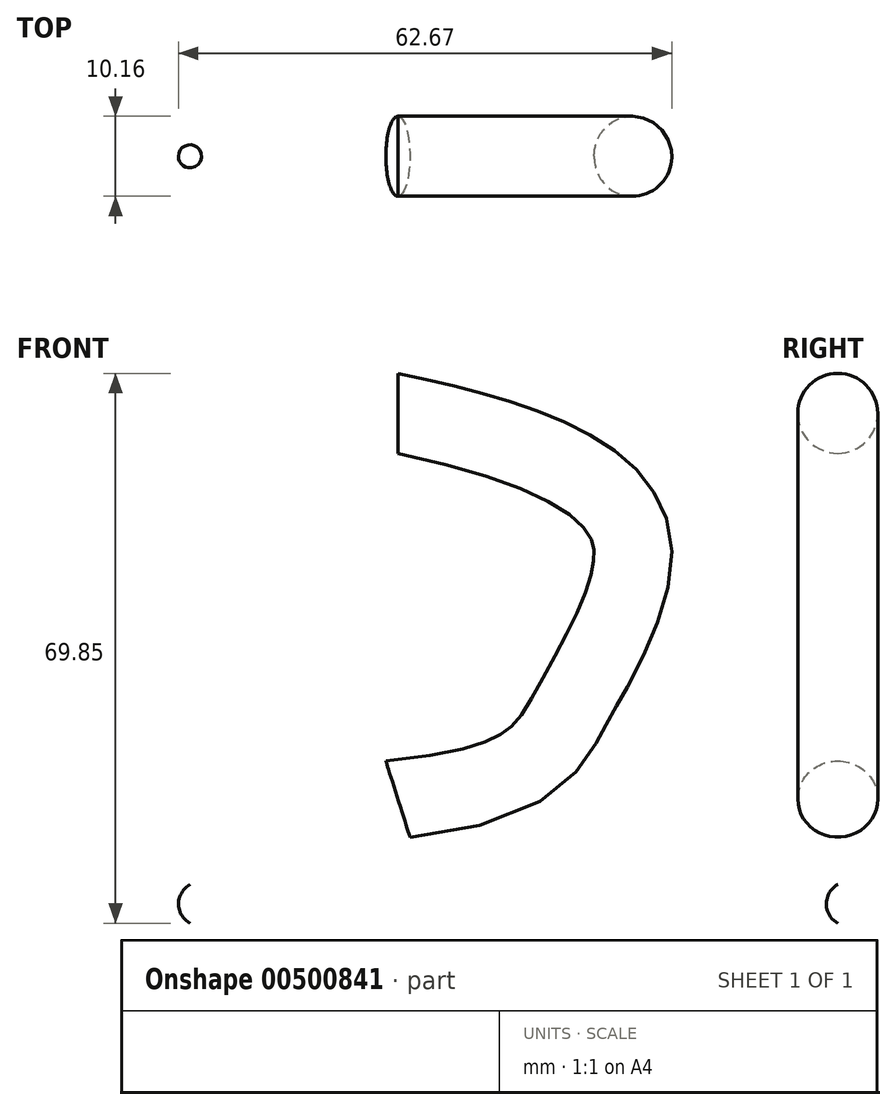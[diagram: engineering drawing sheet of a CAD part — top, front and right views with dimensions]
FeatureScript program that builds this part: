
annotation { "Feature Type Name" : "Feature", "Feature Type Description" : "" }
export const myFeature = defineFeature(function(context is Context, id is Id, definition is map)
    precondition{}
    {
        {
            var Q0;
            Q0=qCreatedBy(makeId("Front.planeOp"),FACE);
            var sketch = newSketch(context, id + "F0", { "sketchPlane" : qUnion([Q0])});
            skFitSpline(sketch, "E0", {"points": [v(0, 0) * mm, v(21.38, 0) * mm, v(22.29, 0) * mm, v(32.23, 23.6) * mm, v(34.34, 76.3) * mm, v(28.91, 76.3) * mm, v(29.21, 58.23) * mm, v(25.9, 24.8) * mm, v(18.37, 6.12) * mm, v(0, 4.92) * mm, v(0, 0) * mm]});
            skLineSegment(sketch, "E1", {"start": v(0, 76.07) * mm, "end": v(0, 0) * mm});
            skSolve(sketch);
        }
        {
            var Q0;
            {var subQ0=sQuery(id+"F0.wireOp",EDGE,"E1");var subQ1=sQuery(id+"F0.wireOp",EDGE,"E0");var subQ2=makeQuery(id+"F0.imprint","INTERSECT",VERTEX,{"disambiguationData":[OD(0.0)],"derivedFrom":[subQ1,subQ0]});Q0=makeQuery(id+"F0.imprint","IMPRINT",FACE,{"disambiguationData":[TD([[makeQuery(id+"F0.imprint","IMPRINT",EDGE,{"disambiguationData":[TD([[subQ2,-1.0]])],"derivedFrom":subQ1}),1.0]])]});}
            var Q1;
            Q1=sQuery(id+"F0.wireOp",EDGE,"E1");
            revolve(context, id + "F1", {"entities" : qUnion([Q0]), "axis" : qUnion([Q1]), "revolveType" : RevolveType.FULL});
        }
        {
            var Q0;
            Q0=qCreatedBy(makeId("Front.planeOp"),FACE);
            var sketch = newSketch(context, id + "F2", { "sketchPlane" : qUnion([Q0])});
            skFitSpline(sketch, "E2", {"points": [v(0, 0) * mm, v(29.7, -16.52) * mm, v(22.58, -36.31) * mm, v(0, -49) * mm], "startDerivative": vector(150.02, -31.37) * mm, "endDerivative": vector(-155.7, -15.6) * mm});
            skSolve(sketch);
        }
        {
            var Q0;
            Q0=qCreatedBy(makeId("Right.planeOp"),FACE);
            var sketch = newSketch(context, id + "F3", { "sketchPlane" : qUnion([Q0])});
            skCircle(sketch, "E3", {"center": v(0, 0) * mm, "radius": 5.08 * mm});
            skSolve(sketch);
        }
        {
            var Q0;
            Q0 = qSketchRegion(id + "F3", true);
            var Q1;
            Q1 = qConstructionFilter(qBodyType(qCreatedBy(id + "F2" ,EDGE), BodyType.WIRE), ConstructionObject.NO);
            sweep(context, id + "F4", {"profiles" : qUnion([Q0]), "path" : qUnion([Q1])});
        }
        {
            var Q0;
            Q0=makeQuery(id+"F4.opSweep","SWEPT_BODY",BODY,{"disambiguationData":[OSD([sQuery(id+"F2.wireOp",EDGE,"E2"),sQuery(id+"F3.wireOp",EDGE,"E3")])]});
            transform(context, id + "F5", {"entities" : qUnion([Q0]), "transformType" : TransformType.TRANSLATION_3D, "dx" : 26.42 * mm, "dy" : 0 * mm, "dz" : 64.77 * mm, "makeCopy" : false});
        }
    });
